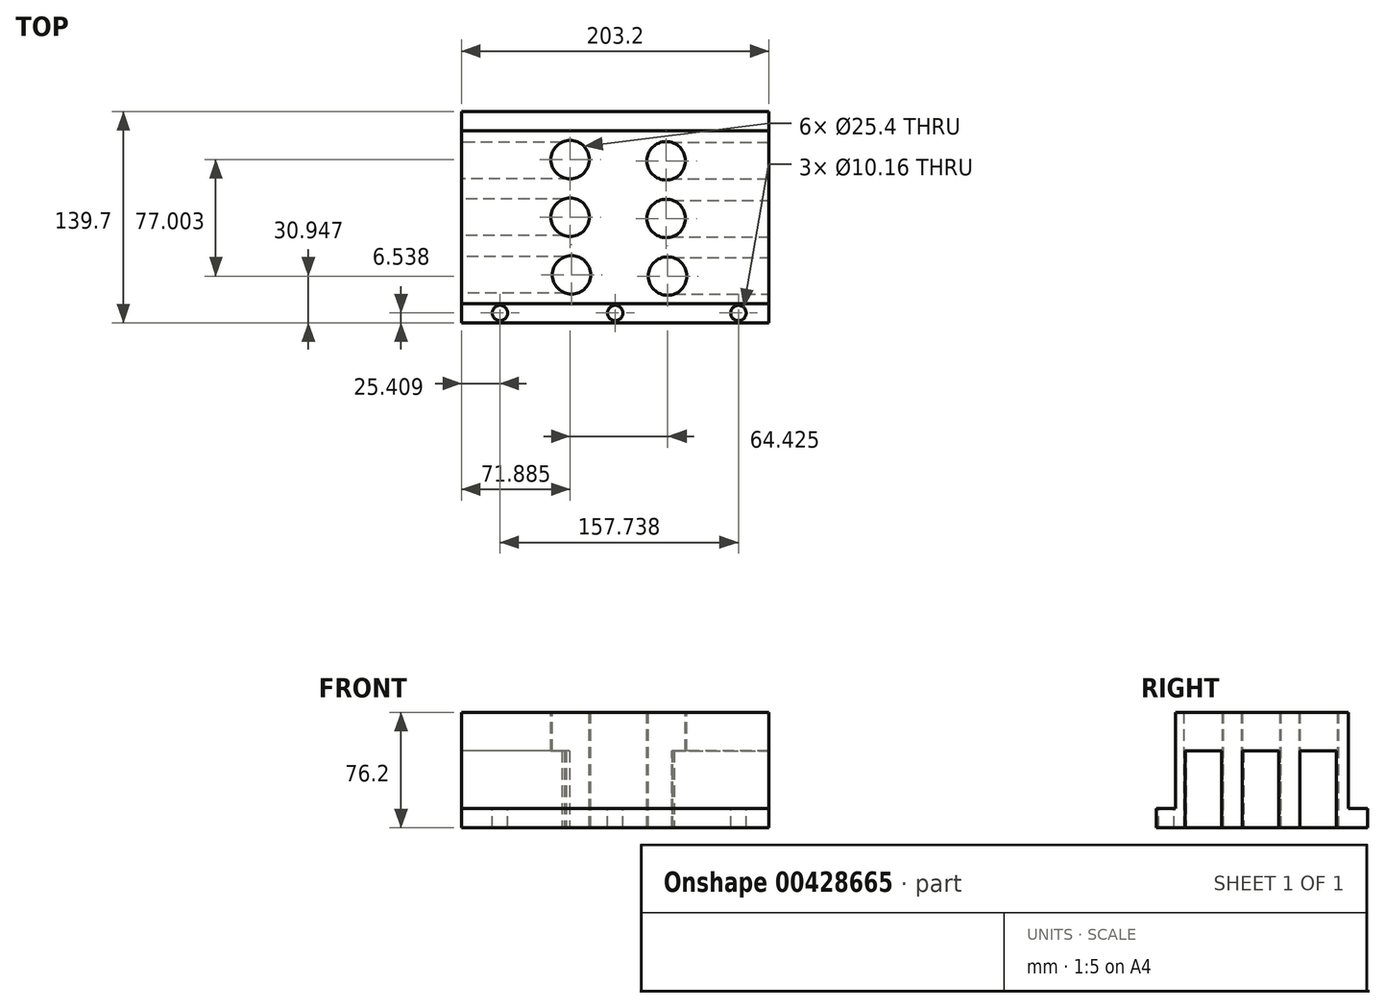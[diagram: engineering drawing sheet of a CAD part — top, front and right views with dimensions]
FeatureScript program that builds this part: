
annotation { "Feature Type Name" : "Feature", "Feature Type Description" : "" }
export const myFeature = defineFeature(function(context is Context, id is Id, definition is map)
    precondition{}
    {
        {
            var Q0;
            Q0=qCreatedBy(makeId("Top.planeOp"),FACE);
            var sketch = newSketch(context, id + "F0", { "sketchPlane" : qUnion([Q0])});
            skLineSegment(sketch, "E0.bottom", {"start": v(-101.6, 57.15) * mm, "end": v(101.6, 57.15) * mm});
            skLineSegment(sketch, "E0.top", {"start": v(-101.6, -57.15) * mm, "end": v(101.6, -57.15) * mm});
            skLineSegment(sketch, "E0.left", {"start": v(-101.6, 57.15) * mm, "end": v(-101.6, -57.15) * mm});
            skLineSegment(sketch, "E0.right", {"start": v(101.6, 57.15) * mm, "end": v(101.6, -57.15) * mm});
            skPoint(sketch, "E0.middle", {"position": v(0, 0) * mm});
            skSolve(sketch);
        }
        {
            var Q0;
            Q0=makeQuery(id+"F0.imprint","IMPRINT",FACE,{"disambiguationData":[TD([[makeQuery(id+"F0.imprint","IMPRINT",EDGE,{"derivedFrom":sQuery(id+"F0.wireOp",EDGE,"E0.bottom")}),-1.0]])]});
            extrude(context, id + "F1", {"entities" : qUnion([Q0]), "depth" : 76.2 * mm});
        }
        {
            var Q0;
            Q0=makeQuery(id+"F1.opExtrude","CAP_FACE",FACE,{"disambiguationData":[OSD([sQuery(id+"F0.wireOp",EDGE,"E0.bottom"),sQuery(id+"F0.wireOp",EDGE,"E0.top"),sQuery(id+"F0.wireOp",EDGE,"E0.left"),sQuery(id+"F0.wireOp",EDGE,"E0.right")])],"isStart":false});
            var sketch = newSketch(context, id + "F2", { "sketchPlane" : qUnion([Q0])});
            skCircle(sketch, "E1", {"center": v(-29.71, 38.1) * mm, "radius": 12.7 * mm});
            skCircle(sketch, "E2", {"center": v(-29.71, 0) * mm, "radius": 12.7 * mm});
            skCircle(sketch, "E3", {"center": v(-28.79, -38.09) * mm, "radius": 12.7 * mm});
            skCircle(sketch, "E4", {"center": v(34.71, -38.9) * mm, "radius": 12.7 * mm});
            skCircle(sketch, "E5", {"center": v(33.79, -0.81) * mm, "radius": 12.7 * mm});
            skCircle(sketch, "E6", {"center": v(33.79, 37.29) * mm, "radius": 12.7 * mm});
            skSolve(sketch);
        }
        {
            var Q0;
            Q0=makeQuery(id+"F2.imprint","IMPRINT",FACE,{"disambiguationData":[TD([[makeQuery(id+"F2.imprint","IMPRINT",EDGE,{"derivedFrom":sQuery(id+"F2.wireOp",EDGE,"E1")}),1.0]])]});
            var Q1;
            Q1=makeQuery(id+"F2.imprint","IMPRINT",FACE,{"disambiguationData":[TD([[makeQuery(id+"F2.imprint","IMPRINT",EDGE,{"derivedFrom":sQuery(id+"F2.wireOp",EDGE,"E2")}),1.0]])]});
            var Q2;
            Q2=makeQuery(id+"F2.imprint","IMPRINT",FACE,{"disambiguationData":[TD([[makeQuery(id+"F2.imprint","IMPRINT",EDGE,{"derivedFrom":sQuery(id+"F2.wireOp",EDGE,"E3")}),1.0]])]});
            var Q3;
            Q3=makeQuery(id+"F2.imprint","IMPRINT",FACE,{"disambiguationData":[TD([[makeQuery(id+"F2.imprint","IMPRINT",EDGE,{"derivedFrom":sQuery(id+"F2.wireOp",EDGE,"E4")}),1.0]])]});
            var Q4;
            Q4=makeQuery(id+"F2.imprint","IMPRINT",FACE,{"disambiguationData":[TD([[makeQuery(id+"F2.imprint","IMPRINT",EDGE,{"derivedFrom":sQuery(id+"F2.wireOp",EDGE,"E5")}),1.0]])]});
            var Q5;
            Q5=makeQuery(id+"F2.imprint","IMPRINT",FACE,{"disambiguationData":[TD([[makeQuery(id+"F2.imprint","IMPRINT",EDGE,{"derivedFrom":sQuery(id+"F2.wireOp",EDGE,"E6")}),1.0]])]});
            extrude(context, id + "F3", {"entities" : qUnion([Q0, Q1, Q2, Q3, Q4, Q5]), "operationType" : NewBodyOperationType.REMOVE, "endBound" : BoundingType.THROUGH_ALL, "oppositeDirection" : true, "depth" : 25.4 * mm});
        }
        {
            var Q0;
            Q0=makeQuery(id+"F1.opExtrude","CAP_FACE",FACE,{"disambiguationData":[OSD([sQuery(id+"F0.wireOp",EDGE,"E0.bottom"),sQuery(id+"F0.wireOp",EDGE,"E0.top"),sQuery(id+"F0.wireOp",EDGE,"E0.left"),sQuery(id+"F0.wireOp",EDGE,"E0.right")])],"isStart":true});
            var sketch = newSketch(context, id + "F4", { "sketchPlane" : qUnion([Q0])});
            skLineSegment(sketch, "E7.bottom", {"start": v(-33.63, -12.08) * mm, "end": v(-101.6, -12.08) * mm});
            skLineSegment(sketch, "E7.top", {"start": v(-33.09, 12.05) * mm, "end": v(-101.6, 12.05) * mm});
            skLineSegment(sketch, "E7.right", {"start": v(-101.6, -12.08) * mm, "end": v(-101.6, 12.05) * mm});
            skLineSegment(sketch, "E8.bottom", {"start": v(-33.04, 26.12) * mm, "end": v(-101.6, 26.12) * mm});
            skLineSegment(sketch, "E8.top", {"start": v(-32.44, 50.25) * mm, "end": v(-101.6, 50.25) * mm});
            skLineSegment(sketch, "E8.right", {"start": v(-101.6, 26.12) * mm, "end": v(-101.6, 50.25) * mm});
            skLineSegment(sketch, "E9.bottom", {"start": v(-35.24, -49.53) * mm, "end": v(-101.6, -49.53) * mm});
            skLineSegment(sketch, "E9.top", {"start": v(-30.07, -25.4) * mm, "end": v(-101.6, -25.4) * mm});
            skLineSegment(sketch, "E9.right", {"start": v(-101.6, -49.53) * mm, "end": v(-101.6, -25.4) * mm});
            skLineSegment(sketch, "E10.bottom", {"start": v(101.6, -49.24) * mm, "end": v(29.49, -49.24) * mm});
            skLineSegment(sketch, "E10.top", {"start": v(101.6, -25.1) * mm, "end": v(30.18, -25.1) * mm});
            skLineSegment(sketch, "E11.bottom", {"start": v(38.12, 26.67) * mm, "end": v(101.6, 26.67) * mm});
            skLineSegment(sketch, "E11.top", {"start": v(39.16, 50.8) * mm, "end": v(101.6, 50.8) * mm});
            skLineSegment(sketch, "E11.right", {"start": v(101.6, 26.67) * mm, "end": v(101.6, 50.8) * mm});
            skLineSegment(sketch, "E12.bottom", {"start": v(29.56, -11.16) * mm, "end": v(101.6, -11.16) * mm});
            skLineSegment(sketch, "E12.top", {"start": v(29.56, 12.97) * mm, "end": v(101.6, 12.97) * mm});
            skLineSegment(sketch, "E12.left", {"start": v(29.56, -11.16) * mm, "end": v(29.56, 12.97) * mm});
            skLineSegment(sketch, "E12.right", {"start": v(101.6, -11.16) * mm, "end": v(101.6, 12.97) * mm});
            skSolve(sketch);
        }
        {
            var Q0;
            {var subQ0=sQuery(id+"F4.wireOp",EDGE,"E8.bottom");Q0=makeQuery(id+"F4.imprint","IMPRINT",FACE,{"disambiguationData":[TD([[makeQuery(id+"F4.imprint","IMPRINT",EDGE,{"derivedFrom":subQ0}),-1.0]])]});}
            var Q1;
            {var subQ0=sQuery(id+"F4.wireOp",EDGE,"E7.bottom");Q1=makeQuery(id+"F4.imprint","IMPRINT",FACE,{"disambiguationData":[TD([[makeQuery(id+"F4.imprint","IMPRINT",EDGE,{"derivedFrom":subQ0}),-1.0]])]});}
            var Q2;
            {var subQ0=sQuery(id+"F4.wireOp",EDGE,"E9.bottom");Q2=makeQuery(id+"F4.imprint","IMPRINT",FACE,{"disambiguationData":[TD([[makeQuery(id+"F4.imprint","IMPRINT",EDGE,{"derivedFrom":subQ0}),-1.0]])]});}
            var Q3;
            {var subQ0=sQuery(id+"F4.wireOp",EDGE,"E10.bottom");Q3=makeQuery(id+"F4.imprint","IMPRINT",FACE,{"disambiguationData":[TD([[makeQuery(id+"F4.imprint","IMPRINT",EDGE,{"derivedFrom":subQ0}),-1.0]])]});}
            var Q4;
            {var subQ4=sQuery(id+"F4.wireOp",EDGE,"E12.bottom");Q4=makeQuery(id+"F4.imprint","IMPRINT",FACE,{"disambiguationData":[TD([[makeQuery(id+"F4.imprint","IMPRINT",EDGE,{"derivedFrom":subQ4}),1.0]])]});}
            var Q5;
            {var subQ0=sQuery(id+"F4.wireOp",EDGE,"E11.bottom");Q5=makeQuery(id+"F4.imprint","IMPRINT",FACE,{"disambiguationData":[TD([[makeQuery(id+"F4.imprint","IMPRINT",EDGE,{"derivedFrom":subQ0}),1.0]])]});}
            extrude(context, id + "F5", {"entities" : qUnion([Q0, Q1, Q2, Q3, Q4, Q5]), "operationType" : NewBodyOperationType.REMOVE, "oppositeDirection" : true, "depth" : 50.8 * mm});
        }
        {
            var Q0;
            Q0=makeQuery(id+"F1.opExtrude","SWEPT_FACE",FACE,{"disambiguationData":[OSD([sQuery(id+"F0.wireOp",EDGE,"E0.top")])]});
            var sketch = newSketch(context, id + "F6", { "sketchPlane" : qUnion([Q0])});
            skLineSegment(sketch, "E13.bottom", {"start": v(-101.6, 0) * mm, "end": v(101.6, 0) * mm});
            skLineSegment(sketch, "E13.top", {"start": v(-101.6, 12.7) * mm, "end": v(101.6, 12.7) * mm});
            skLineSegment(sketch, "E13.left", {"start": v(-101.6, 0) * mm, "end": v(-101.6, 12.7) * mm});
            skLineSegment(sketch, "E13.right", {"start": v(101.6, 0) * mm, "end": v(101.6, 12.7) * mm});
            skSolve(sketch);
        }
        {
            var Q0;
            Q0 = qSketchRegion(id + "F6", true);
            extrude(context, id + "F7", {"entities" : qUnion([Q0]), "operationType" : NewBodyOperationType.ADD, "depth" : 12.7 * mm});
        }
        {
            var Q0;
            Q0=makeQuery(id+"F7.opExtrude","SWEPT_FACE",FACE,{"disambiguationData":[OSD([sQuery(id+"F6.wireOp",EDGE,"E13.top")])]});
            var sketch = newSketch(context, id + "F8", { "sketchPlane" : qUnion([Q0])});
            skCircle(sketch, "E14", {"center": v(-76.2, -63.31) * mm, "radius": 5.08 * mm});
            skCircle(sketch, "E15", {"center": v(0, -63.31) * mm, "radius": 5.08 * mm});
            skCircle(sketch, "E16", {"center": v(81.55, -63.31) * mm, "radius": 5.08 * mm});
            skLineSegment(sketch, "E17", {"start": v(-75.45, 0) * mm, "end": v(80.55, 0) * mm, "construction": true});
            skSolve(sketch);
        }
        {
            var Q0;
            Q0=makeQuery(id+"F1.opExtrude","SWEPT_FACE",FACE,{"disambiguationData":[OSD([sQuery(id+"F0.wireOp",EDGE,"E0.bottom")])]});
            var sketch = newSketch(context, id + "F9", { "sketchPlane" : qUnion([Q0])});
            skLineSegment(sketch, "E18.bottom", {"start": v(-101.6, 0) * mm, "end": v(101.6, 0) * mm});
            skLineSegment(sketch, "E18.top", {"start": v(-101.6, 12.7) * mm, "end": v(101.6, 12.7) * mm});
            skLineSegment(sketch, "E18.left", {"start": v(-101.6, 0) * mm, "end": v(-101.6, 12.7) * mm});
            skLineSegment(sketch, "E18.right", {"start": v(101.6, 0) * mm, "end": v(101.6, 12.7) * mm});
            skSolve(sketch);
        }
        {
            var Q0;
            Q0 = qSketchRegion(id + "F9", true);
            extrude(context, id + "F10", {"entities" : qUnion([Q0]), "operationType" : NewBodyOperationType.ADD, "depth" : 12.7 * mm});
        }
        {
            var Q0;
            Q0=makeQuery(id+"F8.imprint","IMPRINT",FACE,{"disambiguationData":[TD([[makeQuery(id+"F8.imprint","IMPRINT",EDGE,{"derivedFrom":sQuery(id+"F8.wireOp",EDGE,"E14")}),1.0]])]});
            var Q1;
            Q1=makeQuery(id+"F8.imprint","IMPRINT",FACE,{"disambiguationData":[TD([[makeQuery(id+"F8.imprint","IMPRINT",EDGE,{"derivedFrom":sQuery(id+"F8.wireOp",EDGE,"E15")}),1.0]])]});
            var Q2;
            Q2=makeQuery(id+"F8.imprint","IMPRINT",FACE,{"disambiguationData":[TD([[makeQuery(id+"F8.imprint","IMPRINT",EDGE,{"derivedFrom":sQuery(id+"F8.wireOp",EDGE,"E16")}),1.0]])]});
            var Q3;
            Q3=sQuery(id+"F8.wireOp",EDGE,"E16");
            var Q4;
            Q4=sQuery(id+"F8.wireOp",EDGE,"E15");
            var Q5;
            Q5=sQuery(id+"F8.wireOp",EDGE,"E14");
            extrude(context, id + "F11", {"entities" : qUnion([Q0, Q1, Q2]), "operationType" : NewBodyOperationType.REMOVE, "surfaceEntities" : qUnion([Q3, Q4, Q5]), "endBound" : BoundingType.THROUGH_ALL, "oppositeDirection" : true, "depth" : 25.4 * mm});
        }
    });
